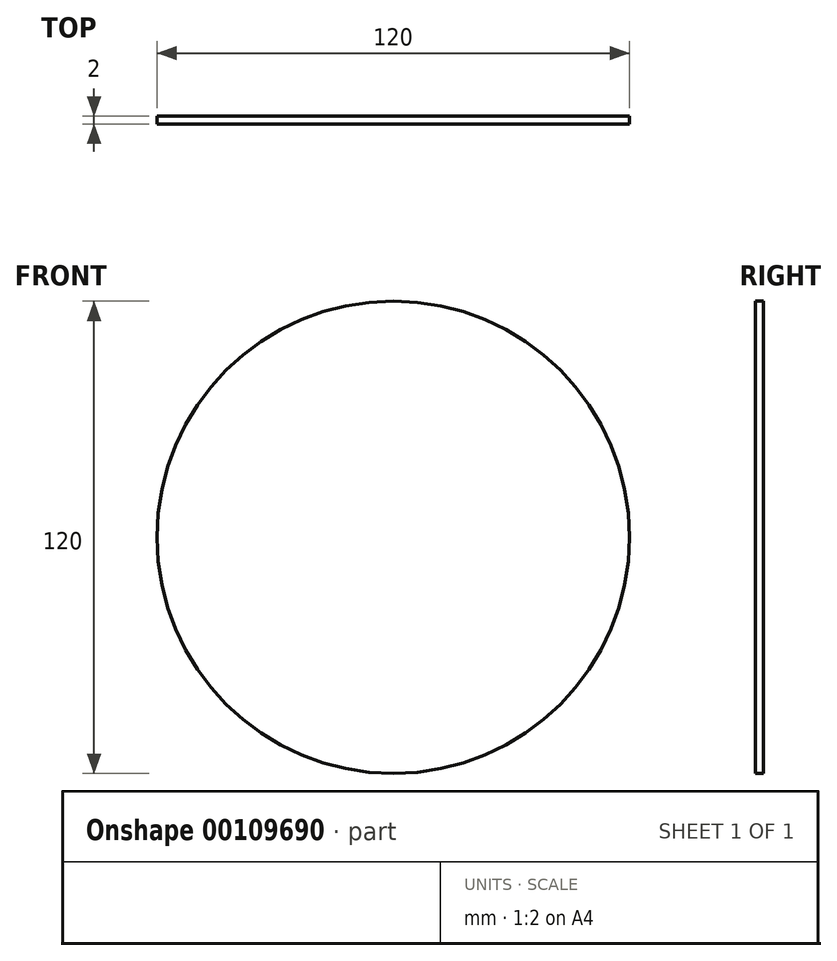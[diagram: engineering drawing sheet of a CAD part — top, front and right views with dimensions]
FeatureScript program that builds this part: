
annotation { "Feature Type Name" : "Feature", "Feature Type Description" : "" }
export const myFeature = defineFeature(function(context is Context, id is Id, definition is map)
    precondition{}
    {
        {
            var Q0;
            Q0=qCreatedBy(makeId("Front.planeOp"),FACE);
            var sketch = newSketch(context, id + "F0", { "sketchPlane" : qUnion([Q0])});
            skCircle(sketch, "E0", {"center": v(0, 0) * mm, "radius": 60 * mm});
            skSolve(sketch);
        }
        {
            var Q0;
            Q0 = qSketchRegion(id + "F0", true);
            extrude(context, id + "F1", {"entities" : qUnion([Q0]), "depth" : 2 * mm});
        }
    });
